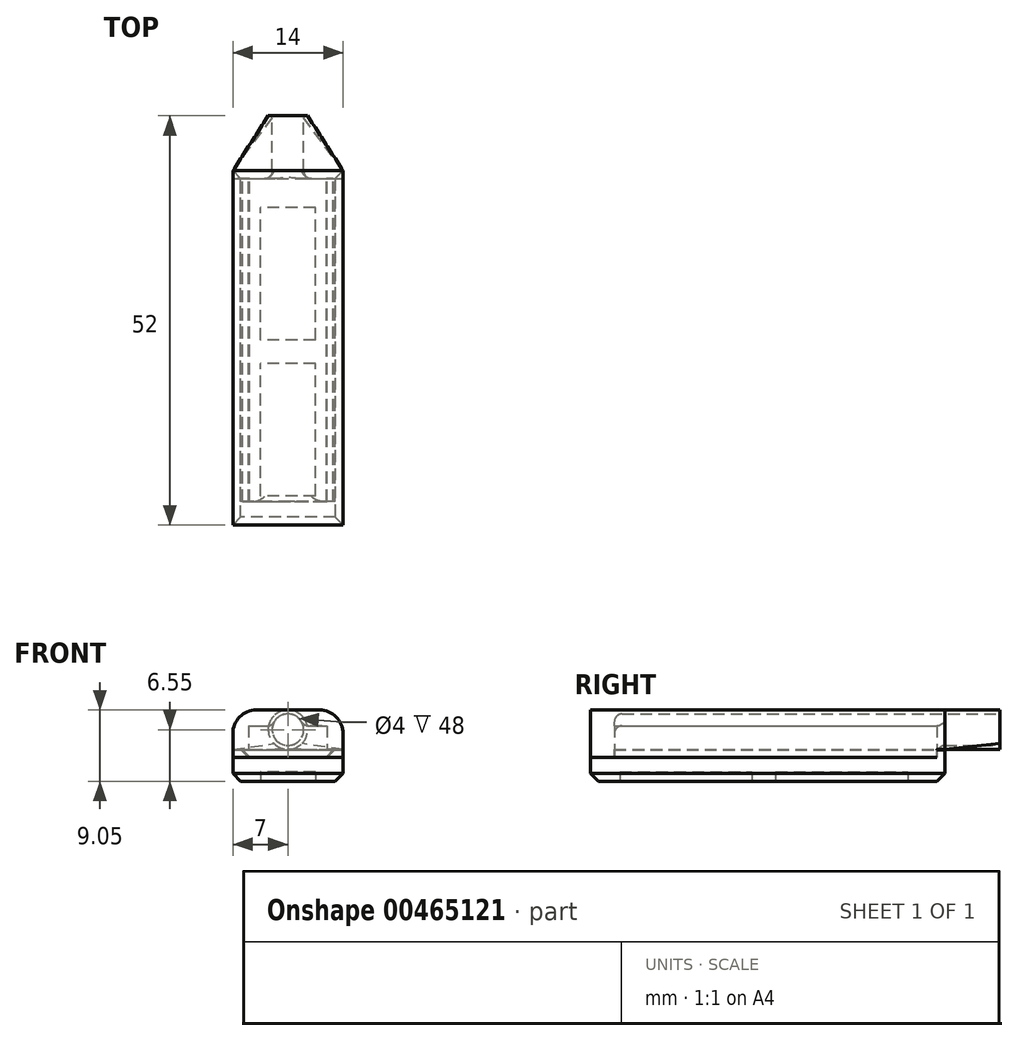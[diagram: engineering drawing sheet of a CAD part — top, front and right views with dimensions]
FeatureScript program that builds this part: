
annotation { "Feature Type Name" : "Feature", "Feature Type Description" : "" }
export const myFeature = defineFeature(function(context is Context, id is Id, definition is map)
    precondition{}
    {
        {
            var Q0;
            Q0=qCreatedBy(makeId("Front.planeOp"),FACE);
            var sketch = newSketch(context, id + "F0", { "sketchPlane" : qUnion([Q0])});
            skLineSegment(sketch, "E0", {"start": v(-5, 0) * mm, "end": v(5, 0) * mm});
            skLineSegment(sketch, "E1", {"start": v(5, 0) * mm, "end": v(5, -4) * mm});
            skLineSegment(sketch, "E2", {"start": v(-5, 0) * mm, "end": v(-5, -4) * mm});
            skLineSegment(sketch, "E3.0", {"start": v(-7, 2) * mm, "end": v(-7, -4) * mm});
            skLineSegment(sketch, "E3.1", {"start": v(-7, 2) * mm, "end": v(7, 2) * mm});
            skLineSegment(sketch, "E3.2", {"start": v(7, 2) * mm, "end": v(7, -4) * mm});
            skLineSegment(sketch, "E4", {"start": v(-7, -4) * mm, "end": v(-5, -4) * mm});
            skLineSegment(sketch, "E5", {"start": v(5, -4) * mm, "end": v(7, -4) * mm});
            skSolve(sketch);
        }
        {
            var Q0;
            Q0 = qSketchRegion(id + "F0", true);
            extrude(context, id + "F1", {"entities" : qUnion([Q0]), "endBound" : BoundingType.SYMMETRIC, "depth" : 44 * mm});
        }
        {
            var Q0;
            Q0=makeQuery(id+"F1.opExtrude","CAP_FACE",FACE,{"disambiguationData":[OSD([sQuery(id+"F0.wireOp",EDGE,"E0"),sQuery(id+"F0.wireOp",EDGE,"E1"),sQuery(id+"F0.wireOp",EDGE,"E2"),sQuery(id+"F0.wireOp",EDGE,"E3.0"),sQuery(id+"F0.wireOp",EDGE,"E3.1"),sQuery(id+"F0.wireOp",EDGE,"E3.2"),sQuery(id+"F0.wireOp",EDGE,"E4"),sQuery(id+"F0.wireOp",EDGE,"E5")])],"isStart":false});
            var sketch = newSketch(context, id + "F2", { "sketchPlane" : qUnion([Q0])});
            skLineSegment(sketch, "E6.bottom", {"start": v(5, 0) * mm, "end": v(-5, 0) * mm});
            skLineSegment(sketch, "E6.top", {"start": v(5, -4) * mm, "end": v(-5, -4) * mm});
            skLineSegment(sketch, "E6.left", {"start": v(5, 0) * mm, "end": v(5, -4) * mm});
            skLineSegment(sketch, "E6.right", {"start": v(-5, 0) * mm, "end": v(-5, -4) * mm});
            skPoint(sketch, "E6.middle", {"position": v(0, -2) * mm});
            skSolve(sketch);
        }
        {
            var Q0;
            Q0=makeQuery(id+"F2.imprint","IMPRINT",FACE,{"disambiguationData":[TD([[makeQuery(id+"F2.imprint","IMPRINT",EDGE,{"derivedFrom":sQuery(id+"F2.wireOp",EDGE,"E6.bottom")}),-1.0]])]});
            extrude(context, id + "F3", {"entities" : qUnion([Q0]), "operationType" : NewBodyOperationType.ADD, "oppositeDirection" : true, "depth" : 3 * mm});
        }
        {
            var Q0;
            Q0=makeQuery(id+"F1.opExtrude","SWEPT_EDGE",EDGE,{"disambiguationData":[OSD([sQuery(id+"F0.wireOp",EDGE,"E3.1"),sQuery(id+"F0.wireOp",EDGE,"E3.2")])]});
            var Q1;
            Q1=makeQuery(id+"F1.opExtrude","SWEPT_EDGE",EDGE,{"disambiguationData":[OSD([sQuery(id+"F0.wireOp",EDGE,"E3.0"),sQuery(id+"F0.wireOp",EDGE,"E3.1")])]});
            fillet(context, id + "F4", {"entities" : qUnion([Q0, Q1]), "radius" : 3 * mm, "tangentPropagation" : true, "allowEdgeOverflow" : false});
        }
        {
            var Q0;
            Q0=makeQuery(id+"F1.opExtrude","CAP_FACE",FACE,{"disambiguationData":[OSD([sQuery(id+"F0.wireOp",EDGE,"E0"),sQuery(id+"F0.wireOp",EDGE,"E1"),sQuery(id+"F0.wireOp",EDGE,"E2"),sQuery(id+"F0.wireOp",EDGE,"E3.0"),sQuery(id+"F0.wireOp",EDGE,"E3.1"),sQuery(id+"F0.wireOp",EDGE,"E3.2"),sQuery(id+"F0.wireOp",EDGE,"E4"),sQuery(id+"F0.wireOp",EDGE,"E5")])],"isStart":true});
            var sketch = newSketch(context, id + "F5", { "sketchPlane" : qUnion([Q0])});
            skLineSegment(sketch, "E7", {"start": v(5, -4) * mm, "end": v(6, -3) * mm});
            skPoint(sketch, "E7.endSnap0", {"position": v(6, -4) * mm});
            skLineSegment(sketch, "E8", {"start": v(6, -3) * mm, "end": v(5, -3) * mm});
            skLineSegment(sketch, "E9", {"start": v(5, -3) * mm, "end": v(5, -4) * mm});
            skLineSegment(sketch, "E10", {"start": v(-5, -4) * mm, "end": v(-6, -3) * mm});
            skPoint(sketch, "E10.endSnap0", {"position": v(-6, -4) * mm});
            skLineSegment(sketch, "E11", {"start": v(-6, -3) * mm, "end": v(-5, -3) * mm});
            skLineSegment(sketch, "E12", {"start": v(-5, -3) * mm, "end": v(-5, -4) * mm});
            skSolve(sketch);
        }
        {
            var Q0;
            Q0 = qSketchRegion(id + "F5", true);
            var Q1;
            Q1=makeQuery(id+"F3.opExtrude","CAP_FACE",FACE,{"disambiguationData":[OSD([sQuery(id+"F2.wireOp",EDGE,"E6.bottom"),sQuery(id+"F2.wireOp",EDGE,"E6.top"),sQuery(id+"F2.wireOp",EDGE,"E6.left"),sQuery(id+"F2.wireOp",EDGE,"E6.right")])],"isStart":false});
            extrude(context, id + "F6", {"entities" : qUnion([Q0]), "operationType" : NewBodyOperationType.REMOVE, "endBound" : BoundingType.UP_TO_SURFACE, "oppositeDirection" : true, "endBoundEntityFace" : qUnion([Q1]), "depth" : 25 * mm});
        }
        {
            var Q0;
            Q0=makeQuery(id+"F1.opExtrude","CAP_FACE",FACE,{"disambiguationData":[OSD([sQuery(id+"F0.wireOp",EDGE,"E0"),sQuery(id+"F0.wireOp",EDGE,"E1"),sQuery(id+"F0.wireOp",EDGE,"E2"),sQuery(id+"F0.wireOp",EDGE,"E3.0"),sQuery(id+"F0.wireOp",EDGE,"E3.1"),sQuery(id+"F0.wireOp",EDGE,"E3.2"),sQuery(id+"F0.wireOp",EDGE,"E4"),sQuery(id+"F0.wireOp",EDGE,"E5")])],"isStart":true});
            var sketch = newSketch(context, id + "F7", { "sketchPlane" : qUnion([Q0])});
            skLineSegment(sketch, "E13.bottom", {"start": v(7, -3) * mm, "end": v(-7, -3) * mm});
            skLineSegment(sketch, "E13.top", {"start": v(7, 2) * mm, "end": v(-7, 2) * mm});
            skLineSegment(sketch, "E13.left", {"start": v(7, -3) * mm, "end": v(7, 2) * mm});
            skLineSegment(sketch, "E13.right", {"start": v(-7, -3) * mm, "end": v(-7, 2) * mm});
            skSolve(sketch);
        }
        {
            var Q0;
            {var subQ2=sQuery(id+"F7.wireOp",EDGE,"E13.bottom");Q0=makeQuery(id+"F7.imprint","IMPRINT",FACE,{"disambiguationData":[TD([[makeQuery(id+"F7.imprint","IMPRINT",EDGE,{"derivedFrom":subQ2}),-1.0]])]});}
            cPlane(context, id + "F8", {"entities" : qUnion([Q0]), "cplaneType" : CPlaneType.OFFSET, "offset" : 8 * mm, "width" : 150 * mm, "height" : 150 * mm});
        }
        {
            var Q0;
            {var subQ5=sQuery(id+"F0.wireOp",EDGE,"E0");Q0=makeQuery(id+"F7.imprint","IMPRINT",FACE,{"disambiguationData":[TD([[makeQuery(id+"F7.imprint","IMPRINT",EDGE,{"derivedFrom":makeQuery(id+"F1.opExtrude","CAP_EDGE",EDGE,{"disambiguationData":[OSD([subQ5])],"isStart":true})}),-1.0]])]});}
            var Q1;
            Q1=makeQuery(id+"F7.imprint","IMPRINT",FACE,{"disambiguationData":[TD([[makeQuery(id+"F7.imprint","IMPRINT",EDGE,{"derivedFrom":makeQuery(id+"F1.opExtrude","CAP_EDGE",EDGE,{"disambiguationData":[OSD([sQuery(id+"F0.wireOp",EDGE,"E0")])],"isStart":true})}),1.0]])]});
            extrude(context, id + "F9", {"entities" : qUnion([Q0, Q1]), "operationType" : NewBodyOperationType.ADD, "depth" : 1 * mm});
        }
        {
            var Q0;
            Q0=qCreatedBy(id+"F8.planeOp",FACE);
            var sketch = newSketch(context, id + "F10", { "sketchPlane" : qUnion([Q0])});
            skLineSegment(sketch, "E14", {"start": v(1.77, 1.27) * mm, "end": v(-1.77, -2.27) * mm, "construction": true});
            skLineSegment(sketch, "E15", {"start": v(1.77, -2.27) * mm, "end": v(-1.77, 1.27) * mm, "construction": true});
            skLineSegment(sketch, "E16", {"start": v(2.45, 0) * mm, "end": v(-2.45, 0) * mm, "construction": true});
            skArc(sketch, "E17", {"start": v(1.77, -2.27) * mm, "mid": v(2.4, -1.22) * mm, "end": v(2.45, 0) * mm});
            skArc(sketch, "E18", {"start": v(-1.77, -2.27) * mm, "mid": v(0, -3) * mm, "end": v(1.77, -2.27) * mm});
            skLineSegment(sketch, "E19", {"start": v(-1.77, 1.27) * mm, "end": v(-1.77, 1.27) * mm});
            skArc(sketch, "E20", {"start": v(1.77, 1.27) * mm, "mid": v(0, 2) * mm, "end": v(-1.77, 1.27) * mm});
            skArc(sketch, "E21", {"start": v(-1.77, 1.27) * mm, "mid": v(-2.2, 0.68) * mm, "end": v(-2.45, 0) * mm});
            skArc(sketch, "E22", {"start": v(2.45, 0) * mm, "mid": v(2.2, 0.68) * mm, "end": v(1.77, 1.27) * mm});
            skArc(sketch, "E23", {"start": v(-2.45, 0) * mm, "mid": v(-2.4, -1.22) * mm, "end": v(-1.77, -2.27) * mm});
            skSolve(sketch);
        }
        {
            var Q1;
            Q1=makeQuery(id+"F9.opExtrude","CAP_FACE",FACE,{"disambiguationData":[OSD([sQuery(id+"F0.wireOp",EDGE,"E0"),sQuery(id+"F0.wireOp",EDGE,"E1"),sQuery(id+"F0.wireOp",EDGE,"E2"),sQuery(id+"F0.wireOp",EDGE,"E3.0"),sQuery(id+"F0.wireOp",EDGE,"E3.1"),sQuery(id+"F0.wireOp",EDGE,"E3.2"),sQuery(id+"F0.wireOp",EDGE,"E4"),sQuery(id+"F0.wireOp",EDGE,"E5"),sQuery(id+"F7.wireOp",EDGE,"E13.bottom"),sQuery(id+"F7.wireOp",EDGE,"E13.top"),sQuery(id+"F7.wireOp",EDGE,"E13.left"),sQuery(id+"F7.wireOp",EDGE,"E13.right")])],"isStart":false});
            var Q2;
            Q2=makeQuery(id+"F10.imprint","IMPRINT",FACE,{"disambiguationData":[TD([[makeQuery(id+"F10.imprint","IMPRINT",EDGE,{"derivedFrom":sQuery(id+"F10.wireOp",EDGE,"E17")}),1.0]])]});
            loft(context, id + "F11", {"operationType" : NewBodyOperationType.ADD, "sheetProfilesArray" : [{ "sheetProfileEntities" : qUnion([Q1]) }, { "sheetProfileEntities" : qUnion([Q2]) }]});
        }
        {
            var Q0;
            Q0=makeQuery(id+"F11.opLoft","CAP_FACE",FACE,{"disambiguationData":[OSD([makeQuery(id+"F10.imprint","IMPRINT",FACE,{"disambiguationData":[TD([[makeQuery(id+"F10.imprint","IMPRINT",EDGE,{"derivedFrom":sQuery(id+"F10.wireOp",EDGE,"E17")}),1.0]])]})])],"isStart":true});
            var sketch = newSketch(context, id + "F12", { "sketchPlane" : qUnion([Q0])});
            skCircle(sketch, "E24", {"center": v(0, -0.5) * mm, "radius": 2 * mm});
            skSolve(sketch);
        }
        {
            var Q0;
            Q0=makeQuery(id+"F12.imprint","IMPRINT",FACE,{"disambiguationData":[TD([[makeQuery(id+"F12.imprint","IMPRINT",EDGE,{"derivedFrom":sQuery(id+"F12.wireOp",EDGE,"E24")}),1.0]])]});
            var Q1;
            Q1=makeQuery(id+"F6.boolean.opBoolean","MERGE",FACE,{"derivedFrom":[makeQuery(id+"F3.opExtrude","CAP_FACE",FACE,{"disambiguationData":[OSD([sQuery(id+"F2.wireOp",EDGE,"E6.bottom"),sQuery(id+"F2.wireOp",EDGE,"E6.top"),sQuery(id+"F2.wireOp",EDGE,"E6.left"),sQuery(id+"F2.wireOp",EDGE,"E6.right")])],"isStart":false})],"fromTools":[makeQuery(id+"F6.opExtrude","CAP_FACE",FACE,{"disambiguationData":[OSD([sQuery(id+"F5.wireOp",EDGE,"E7"),sQuery(id+"F5.wireOp",EDGE,"E8"),sQuery(id+"F5.wireOp",EDGE,"E9")])],"isStart":false}),makeQuery(id+"F6.opExtrude","CAP_FACE",FACE,{"disambiguationData":[OSD([sQuery(id+"F5.wireOp",EDGE,"E10"),sQuery(id+"F5.wireOp",EDGE,"E11"),sQuery(id+"F5.wireOp",EDGE,"E12")])],"isStart":false})]});
            extrude(context, id + "F13", {"entities" : qUnion([Q0]), "operationType" : NewBodyOperationType.REMOVE, "endBound" : BoundingType.UP_TO_SURFACE, "oppositeDirection" : true, "endBoundEntityFace" : qUnion([Q1]), "depth" : 36.6 * mm});
        }
        {
            var Q0;
            Q0=makeQuery(id+"F13.boolean.opBoolean","INTERSECT",EDGE,{"disambiguationData":[OD(0.0)],"derivedFrom":[makeQuery(id+"F1.opExtrude","SWEPT_FACE",FACE,{"disambiguationData":[OSD([sQuery(id+"F0.wireOp",EDGE,"E0")])]}),makeQuery(id+"F13.opExtrude","SWEPT_FACE",FACE,{"disambiguationData":[OSD([sQuery(id+"F12.wireOp",EDGE,"E24")])]})]});
            var Q1;
            Q1=makeQuery(id+"F13.boolean.opBoolean","INTERSECT",EDGE,{"disambiguationData":[OD(1.0)],"derivedFrom":[makeQuery(id+"F1.opExtrude","SWEPT_FACE",FACE,{"disambiguationData":[OSD([sQuery(id+"F0.wireOp",EDGE,"E0")])]}),makeQuery(id+"F13.opExtrude","SWEPT_FACE",FACE,{"disambiguationData":[OSD([sQuery(id+"F12.wireOp",EDGE,"E24")])]})]});
            var Q2;
            Q2=makeQuery(id+"F13.boolean.opBoolean","COPY",EDGE,{"derivedFrom":makeQuery(id+"F13.opExtrude","CAP_EDGE",EDGE,{"disambiguationData":[OSD([sQuery(id+"F12.wireOp",EDGE,"E24")])],"isStart":false})});
            var Q3;
            Q3=makeQuery(id+"F13.boolean.opBoolean","INTERSECT",EDGE,{"derivedFrom":[makeQuery(id+"F9.opExtrude","CAP_FACE",FACE,{"disambiguationData":[OSD([sQuery(id+"F0.wireOp",EDGE,"E0"),sQuery(id+"F0.wireOp",EDGE,"E1"),sQuery(id+"F0.wireOp",EDGE,"E2"),sQuery(id+"F0.wireOp",EDGE,"E3.0"),sQuery(id+"F0.wireOp",EDGE,"E3.1"),sQuery(id+"F0.wireOp",EDGE,"E3.2"),sQuery(id+"F0.wireOp",EDGE,"E4"),sQuery(id+"F0.wireOp",EDGE,"E5"),sQuery(id+"F7.wireOp",EDGE,"E13.bottom"),sQuery(id+"F7.wireOp",EDGE,"E13.top"),sQuery(id+"F7.wireOp",EDGE,"E13.left"),sQuery(id+"F7.wireOp",EDGE,"E13.right")])],"isStart":true}),makeQuery(id+"F13.opExtrude","SWEPT_FACE",FACE,{"disambiguationData":[OSD([sQuery(id+"F12.wireOp",EDGE,"E24")])]})]});
            fillet(context, id + "F14", {"entities" : qUnion([Q0, Q1, Q2, Q3]), "radius" : 1 * mm, "tangentPropagation" : true, "allowEdgeOverflow" : false});
        }
        {
            var Q0;
            {var subQ0=sQuery(id+"F0.wireOp",EDGE,"E5");var subQ1=sQuery(id+"F0.wireOp",EDGE,"E4");var subQ2=sQuery(id+"F0.wireOp",EDGE,"E3.0");Q0=makeQuery(id+"F9.boolean.opBoolean","SPLIT",FACE,{"disambiguationData":[TD([makeQuery(id+"F1.opExtrude","SWEPT_FACE",FACE,{"disambiguationData":[OSD([subQ2])]})])],"derivedFrom":makeQuery(id+"F1.opExtrude","CAP_FACE",FACE,{"disambiguationData":[OSD([sQuery(id+"F0.wireOp",EDGE,"E0"),sQuery(id+"F0.wireOp",EDGE,"E1"),sQuery(id+"F0.wireOp",EDGE,"E2"),subQ2,sQuery(id+"F0.wireOp",EDGE,"E3.1"),sQuery(id+"F0.wireOp",EDGE,"E3.2"),subQ1,subQ0])],"isStart":true})});}
            var sketch = newSketch(context, id + "F15", { "sketchPlane" : qUnion([Q0])});
            skLineSegment(sketch, "E25", {"start": v(0, 0) * mm, "end": v(0, -7.28) * mm, "construction": true});
            skLineSegment(sketch, "E26", {"start": v(5.76, -3.1) * mm, "end": v(4.9, -3.96) * mm});
            skLineSegment(sketch, "E27", {"start": v(4.9, -3.96) * mm, "end": v(4.9, -4.05) * mm});
            skLineSegment(sketch, "E28", {"start": v(4.9, -4.05) * mm, "end": v(7, -4.05) * mm});
            skLineSegment(sketch, "E29", {"start": v(7, -4.05) * mm, "end": v(7, -7.05) * mm});
            skLineSegment(sketch, "E30", {"start": v(7, -7.05) * mm, "end": v(0, -7.05) * mm});
            skLineSegment(sketch, "E31", {"start": v(5.76, -3.1) * mm, "end": v(0, -3.1) * mm});
            skLineSegment(sketch, "E32.MirrorCS", {"start": v(-5.76, -3.1) * mm, "end": v(0, -3.1) * mm});
            skLineSegment(sketch, "E33.MirrorCS", {"start": v(-5.76, -3.1) * mm, "end": v(-4.9, -3.96) * mm});
            skLineSegment(sketch, "E34.MirrorCS", {"start": v(-4.9, -3.96) * mm, "end": v(-4.9, -4.05) * mm});
            skLineSegment(sketch, "E35.MirrorCS", {"start": v(-4.9, -4.05) * mm, "end": v(-7, -4.05) * mm});
            skLineSegment(sketch, "E36.MirrorCS", {"start": v(-7, -4.05) * mm, "end": v(-7, -7.05) * mm});
            skLineSegment(sketch, "E37.MirrorCS", {"start": v(-7, -7.05) * mm, "end": v(0, -7.05) * mm});
            skSolve(sketch);
        }
        {
            var Q0;
            Q0=makeQuery(id+"F15.imprint","IMPRINT",FACE,{"disambiguationData":[TD([[makeQuery(id+"F15.imprint","IMPRINT",EDGE,{"derivedFrom":sQuery(id+"F15.wireOp",EDGE,"E26")}),-1.0]])]});
            var Q1;
            Q1=makeQuery(id+"F13.boolean.opBoolean","MERGE",FACE,{"derivedFrom":[makeQuery(id+"F6.boolean.opBoolean","MERGE",FACE,{"derivedFrom":[makeQuery(id+"F3.opExtrude","CAP_FACE",FACE,{"disambiguationData":[OSD([sQuery(id+"F2.wireOp",EDGE,"E6.bottom"),sQuery(id+"F2.wireOp",EDGE,"E6.top"),sQuery(id+"F2.wireOp",EDGE,"E6.left"),sQuery(id+"F2.wireOp",EDGE,"E6.right")])],"isStart":false})],"fromTools":[makeQuery(id+"F6.opExtrude","CAP_FACE",FACE,{"disambiguationData":[OSD([sQuery(id+"F5.wireOp",EDGE,"E7"),sQuery(id+"F5.wireOp",EDGE,"E8"),sQuery(id+"F5.wireOp",EDGE,"E9")])],"isStart":false}),makeQuery(id+"F6.opExtrude","CAP_FACE",FACE,{"disambiguationData":[OSD([sQuery(id+"F5.wireOp",EDGE,"E10"),sQuery(id+"F5.wireOp",EDGE,"E11"),sQuery(id+"F5.wireOp",EDGE,"E12")])],"isStart":false})]})],"fromTools":[makeQuery(id+"F13.opExtrude","CAP_FACE",FACE,{"disambiguationData":[OSD([sQuery(id+"F12.wireOp",EDGE,"E24")])],"isStart":false})]});
            extrude(context, id + "F16", {"entities" : qUnion([Q0]), "endBound" : BoundingType.UP_TO_SURFACE, "oppositeDirection" : true, "endBoundEntityFace" : qUnion([Q1]), "depth" : 25 * mm});
        }
        {
            var Q0;
            Q0=makeQuery(id+"F16.opExtrude","CAP_FACE",FACE,{"disambiguationData":[OSD([sQuery(id+"F15.wireOp",EDGE,"E26"),sQuery(id+"F15.wireOp",EDGE,"E27"),sQuery(id+"F15.wireOp",EDGE,"E28"),sQuery(id+"F15.wireOp",EDGE,"E29"),sQuery(id+"F15.wireOp",EDGE,"E30"),sQuery(id+"F15.wireOp",EDGE,"E31"),sQuery(id+"F15.wireOp",EDGE,"E32.MirrorCS"),sQuery(id+"F15.wireOp",EDGE,"E33.MirrorCS"),sQuery(id+"F15.wireOp",EDGE,"E34.MirrorCS"),sQuery(id+"F15.wireOp",EDGE,"E35.MirrorCS"),sQuery(id+"F15.wireOp",EDGE,"E36.MirrorCS"),sQuery(id+"F15.wireOp",EDGE,"E37.MirrorCS")])],"isStart":false});
            var sketch = newSketch(context, id + "F17", { "sketchPlane" : qUnion([Q0])});
            skLineSegment(sketch, "E38.bottom", {"start": v(-7, -4.05) * mm, "end": v(7, -4.05) * mm});
            skLineSegment(sketch, "E38.top", {"start": v(-7, -7.05) * mm, "end": v(7, -7.05) * mm});
            skLineSegment(sketch, "E38.left", {"start": v(-7, -4.05) * mm, "end": v(-7, -7.05) * mm});
            skLineSegment(sketch, "E38.right", {"start": v(7, -4.05) * mm, "end": v(7, -7.05) * mm});
            skSolve(sketch);
        }
        {
            var Q0;
            Q0=makeQuery(id+"F17.imprint","IMPRINT",FACE,{"disambiguationData":[TD([[makeQuery(id+"F17.imprint","IMPRINT",EDGE,{"derivedFrom":sQuery(id+"F17.wireOp",EDGE,"E38.top")}),-1.0]])]});
            var Q1;
            Q1=makeQuery(id+"F3.boolean.opBoolean","MERGE",FACE,{"derivedFrom":[makeQuery(id+"F1.opExtrude","CAP_FACE",FACE,{"disambiguationData":[OSD([sQuery(id+"F0.wireOp",EDGE,"E0"),sQuery(id+"F0.wireOp",EDGE,"E1"),sQuery(id+"F0.wireOp",EDGE,"E2"),sQuery(id+"F0.wireOp",EDGE,"E3.0"),sQuery(id+"F0.wireOp",EDGE,"E3.1"),sQuery(id+"F0.wireOp",EDGE,"E3.2"),sQuery(id+"F0.wireOp",EDGE,"E4"),sQuery(id+"F0.wireOp",EDGE,"E5")])],"isStart":false}),makeQuery(id+"F3.opExtrude","CAP_FACE",FACE,{"disambiguationData":[OSD([sQuery(id+"F2.wireOp",EDGE,"E6.bottom"),sQuery(id+"F2.wireOp",EDGE,"E6.top"),sQuery(id+"F2.wireOp",EDGE,"E6.left"),sQuery(id+"F2.wireOp",EDGE,"E6.right")])],"isStart":true})]});
            extrude(context, id + "F18", {"entities" : qUnion([Q0]), "operationType" : NewBodyOperationType.ADD, "endBound" : BoundingType.UP_TO_SURFACE, "endBoundEntityFace" : qUnion([Q1]), "depth" : 25 * mm});
        }
        {
            var Q0;
            Q0=makeQuery(id+"F16.opExtrude","CAP_FACE",FACE,{"disambiguationData":[OSD([sQuery(id+"F15.wireOp",EDGE,"E26"),sQuery(id+"F15.wireOp",EDGE,"E27"),sQuery(id+"F15.wireOp",EDGE,"E28"),sQuery(id+"F15.wireOp",EDGE,"E29"),sQuery(id+"F15.wireOp",EDGE,"E30"),sQuery(id+"F15.wireOp",EDGE,"E31"),sQuery(id+"F15.wireOp",EDGE,"E32.MirrorCS"),sQuery(id+"F15.wireOp",EDGE,"E33.MirrorCS"),sQuery(id+"F15.wireOp",EDGE,"E34.MirrorCS"),sQuery(id+"F15.wireOp",EDGE,"E35.MirrorCS"),sQuery(id+"F15.wireOp",EDGE,"E36.MirrorCS"),sQuery(id+"F15.wireOp",EDGE,"E37.MirrorCS")])],"isStart":true});
            var sketch = newSketch(context, id + "F19", { "sketchPlane" : qUnion([Q0])});
            skLineSegment(sketch, "E39.bottom", {"start": v(7, -7.05) * mm, "end": v(-7, -7.05) * mm});
            skLineSegment(sketch, "E39.top", {"start": v(7, -3.1) * mm, "end": v(-7, -3.1) * mm});
            skLineSegment(sketch, "E39.left", {"start": v(7, -7.05) * mm, "end": v(7, -3.1) * mm});
            skLineSegment(sketch, "E39.right", {"start": v(-7, -7.05) * mm, "end": v(-7, -3.1) * mm});
            skSolve(sketch);
        }
        {
            var Q0;
            Q0 = qSketchRegion(id + "F19", true);
            extrude(context, id + "F20", {"entities" : qUnion([Q0]), "operationType" : NewBodyOperationType.ADD, "depth" : 1 * mm});
        }
        {
            var Q0;
            Q0=makeQuery(id+"F20.boolean.opBoolean","MERGE",FACE,{"derivedFrom":[makeQuery(id+"F18.boolean.opBoolean","MERGE",FACE,{"derivedFrom":[makeQuery(id+"F16.opExtrude","SWEPT_FACE",FACE,{"disambiguationData":[OSD([sQuery(id+"F15.wireOp",EDGE,"E30"),sQuery(id+"F15.wireOp",EDGE,"E37.MirrorCS")])]}),makeQuery(id+"F18.opExtrude","SWEPT_FACE",FACE,{"disambiguationData":[OSD([sQuery(id+"F17.wireOp",EDGE,"E38.top")])]})]}),makeQuery(id+"F20.opExtrude","SWEPT_FACE",FACE,{"disambiguationData":[OSD([sQuery(id+"F19.wireOp",EDGE,"E39.bottom")])]})]});
            chamfer(context, id + "F21", {"entities" : qUnion([Q0]), "width" : 1 * mm, "tangentPropagation" : true});
        }
        {
            var Q0;
            Q0=makeQuery(id+"F20.boolean.opBoolean","MERGE",FACE,{"derivedFrom":[makeQuery(id+"F18.boolean.opBoolean","MERGE",FACE,{"derivedFrom":[makeQuery(id+"F16.opExtrude","SWEPT_FACE",FACE,{"disambiguationData":[OSD([sQuery(id+"F15.wireOp",EDGE,"E30"),sQuery(id+"F15.wireOp",EDGE,"E37.MirrorCS")])]}),makeQuery(id+"F18.opExtrude","SWEPT_FACE",FACE,{"disambiguationData":[OSD([sQuery(id+"F17.wireOp",EDGE,"E38.top")])]})]}),makeQuery(id+"F20.opExtrude","SWEPT_FACE",FACE,{"disambiguationData":[OSD([sQuery(id+"F19.wireOp",EDGE,"E39.bottom")])]})]});
            var sketch = newSketch(context, id + "F22", { "sketchPlane" : qUnion([Q0])});
            skLineSegment(sketch, "E40.bottom", {"start": v(3.5, 18.3) * mm, "end": v(-3.5, 18.3) * mm});
            skLineSegment(sketch, "E40.top", {"start": v(3.5, 1.5) * mm, "end": v(-3.5, 1.5) * mm});
            skLineSegment(sketch, "E40.left", {"start": v(3.5, 18.3) * mm, "end": v(3.5, 1.5) * mm});
            skLineSegment(sketch, "E40.right", {"start": v(-3.5, 18.3) * mm, "end": v(-3.5, 1.5) * mm});
            skLineSegment(sketch, "E41.bottom", {"start": v(3.5, -1.5) * mm, "end": v(-3.5, -1.5) * mm});
            skLineSegment(sketch, "E41.top", {"start": v(3.5, -18.3) * mm, "end": v(-3.5, -18.3) * mm});
            skLineSegment(sketch, "E41.left", {"start": v(3.5, -1.5) * mm, "end": v(3.5, -18.3) * mm});
            skLineSegment(sketch, "E41.right", {"start": v(-3.5, -1.5) * mm, "end": v(-3.5, -18.3) * mm});
            skLineSegment(sketch, "E42", {"start": v(0, 5.89) * mm, "end": v(0, -9.26) * mm, "construction": true});
            skLineSegment(sketch, "E43", {"start": v(4.85, 0) * mm, "end": v(-4.98, 0) * mm, "construction": true});
            skSolve(sketch);
        }
        {
            var Q0;
            Q0=makeQuery(id+"F22.imprint","IMPRINT",FACE,{"disambiguationData":[TD([[makeQuery(id+"F22.imprint","IMPRINT",EDGE,{"derivedFrom":sQuery(id+"F22.wireOp",EDGE,"E40.bottom")}),1.0]])]});
            var Q1;
            Q1=makeQuery(id+"F22.imprint","IMPRINT",FACE,{"disambiguationData":[TD([[makeQuery(id+"F22.imprint","IMPRINT",EDGE,{"derivedFrom":sQuery(id+"F22.wireOp",EDGE,"E41.bottom")}),1.0]])]});
            extrude(context, id + "F23", {"entities" : qUnion([Q0, Q1]), "operationType" : NewBodyOperationType.REMOVE, "oppositeDirection" : true, "depth" : 1.2 * mm});
        }
    });
